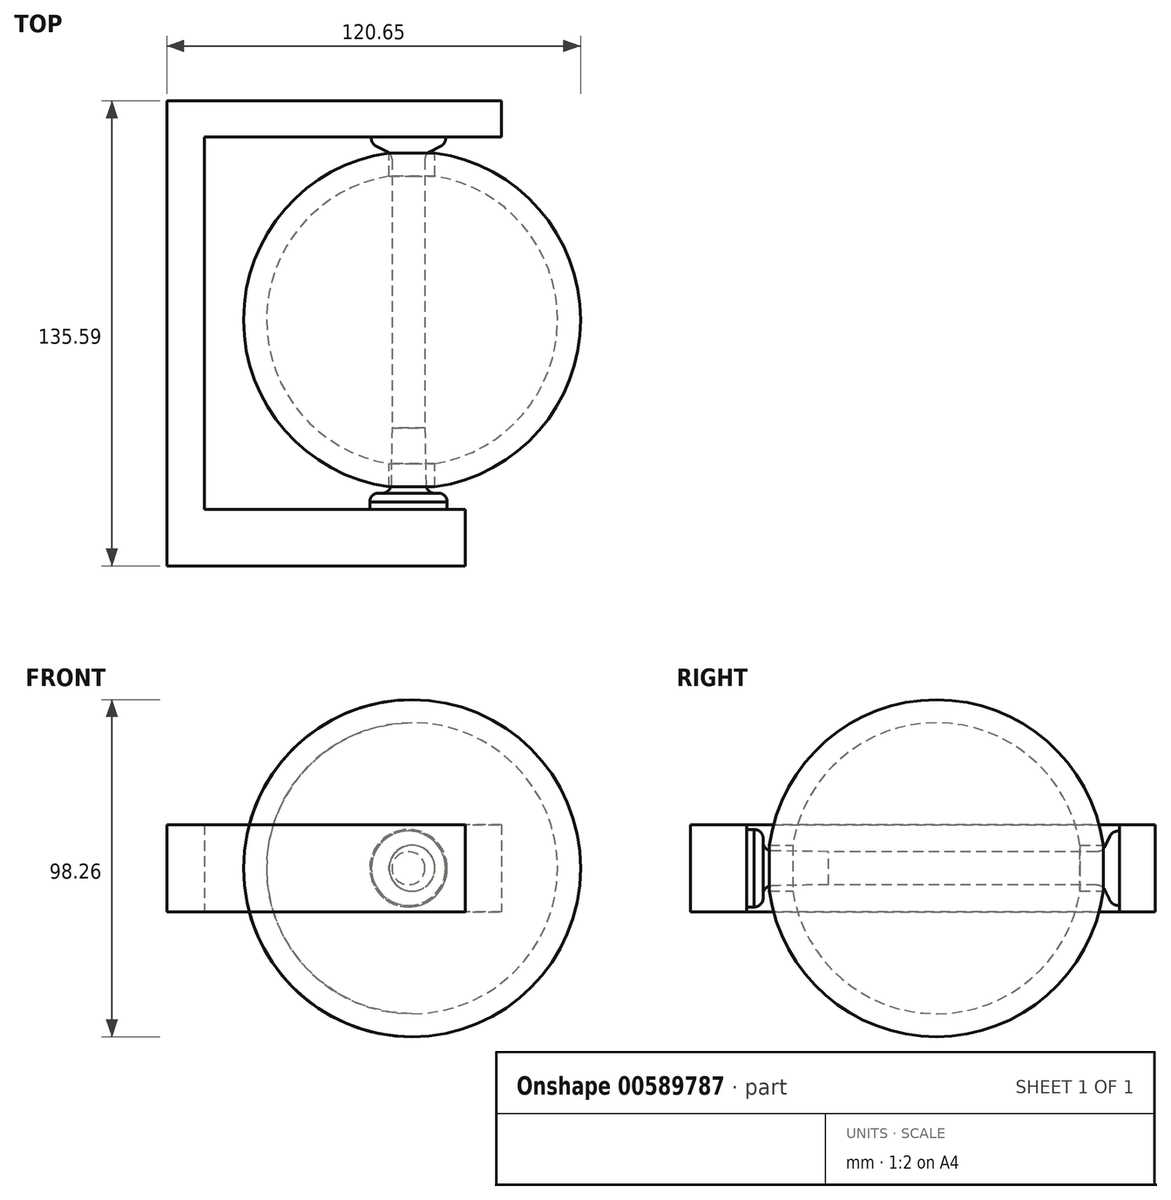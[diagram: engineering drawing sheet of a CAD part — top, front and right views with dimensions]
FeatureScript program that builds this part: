
annotation { "Feature Type Name" : "Feature", "Feature Type Description" : "" }
export const myFeature = defineFeature(function(context is Context, id is Id, definition is map)
    precondition{}
    {
        {
            var Q0;
            Q0=qCreatedBy(makeId("Front.planeOp"),FACE);
            var sketch = newSketch(context, id + "F0", { "sketchPlane" : qUnion([Q0])});
            skArc(sketch, "E0", {"start": v(0, -47.4) * mm, "mid": v(47.4, 0) * mm, "end": v(0, 47.4) * mm});
            skCircle(sketch, "E1", {"center": v(0, 0) * mm, "radius": 42.42 * mm});
            skLineSegment(sketch, "E2.trimOffspring", {"start": v(0, -42.42) * mm, "end": v(0, -47.4) * mm});
            skPoint(sketch, "E3.start.orphan", {"position": v(0, 47.4) * mm});
            skLineSegment(sketch, "E4", {"start": v(0, 47.4) * mm, "end": v(0, 42.42) * mm});
            skCircle(sketch, "E5", {"center": v(0, 0) * mm, "radius": 49.13 * mm});
            skLineSegment(sketch, "E6", {"start": v(0, 47.4) * mm, "end": v(0, 49.13) * mm});
            skLineSegment(sketch, "E7", {"start": v(0, -47.4) * mm, "end": v(0, -49.13) * mm});
            skSolve(sketch);
        }
        {
            var Q0;
            {var subQ4=sQuery(id+"F0.wireOp",EDGE,"E2.trimOffspring");Q0=makeQuery(id+"F0.imprint","IMPRINT",FACE,{"disambiguationData":[TD([[makeQuery(id+"F0.imprint","IMPRINT",EDGE,{"derivedFrom":subQ4}),-1.0]])]});}
            var Q1;
            Q1=sQuery(id+"F0.wireOp",EDGE,"E4");
            revolve(context, id + "F1", {"entities" : qUnion([Q0]), "axis" : qUnion([Q1]), "revolveType" : RevolveType.FULL});
        }
        {
            var Q0;
            Q0=qCreatedBy(makeId("Front.planeOp"),FACE);
            var sketch = newSketch(context, id + "F2", { "sketchPlane" : qUnion([Q0])});
            skCircle(sketch, "E8", {"center": v(0, 0) * mm, "radius": 6.69 * mm});
            skSolve(sketch);
        }
        {
            var Q0;
            Q0 = qSketchRegion(id + "F2", true);
            var Q1;
            Q1=sQuery(id+"F2.wireOp",EDGE,"E8");
            extrude(context, id + "F3", {"entities" : qUnion([Q0]), "operationType" : NewBodyOperationType.REMOVE, "surfaceEntities" : qUnion([Q1]), "endBound" : BoundingType.SYMMETRIC, "depth" : 118.87 * mm, "offsetDistance" : 25.4 * mm});
        }
        {
            var Q0;
            Q0=qCreatedBy(makeId("Top.planeOp"),FACE);
            var sketch = newSketch(context, id + "F4", { "sketchPlane" : qUnion([Q0])});
            skLineSegment(sketch, "E9", {"start": v(15.54, -66.32) * mm, "end": v(15.54, -55.32) * mm});
            skLineSegment(sketch, "E10", {"start": v(15.54, -55.32) * mm, "end": v(-60.54, -55.32) * mm});
            skLineSegment(sketch, "E11", {"start": v(-60.54, -55.32) * mm, "end": v(-60.54, 53.34) * mm});
            skLineSegment(sketch, "E12", {"start": v(-60.54, 53.34) * mm, "end": v(26.1, 53.34) * mm});
            skLineSegment(sketch, "E13", {"start": v(26.1, 53.34) * mm, "end": v(26.1, 63.84) * mm});
            skLineSegment(sketch, "E14", {"start": v(26.1, 63.84) * mm, "end": v(-71.52, 63.84) * mm});
            skLineSegment(sketch, "E15", {"start": v(-71.52, 63.84) * mm, "end": v(-71.52, -71.75) * mm});
            skLineSegment(sketch, "E16", {"start": v(-71.52, -71.75) * mm, "end": v(15.54, -71.75) * mm});
            skLineSegment(sketch, "E17", {"start": v(15.54, -71.75) * mm, "end": v(15.54, -66.32) * mm});
            skSolve(sketch);
        }
        {
            var Q0;
            Q0=qCreatedBy(makeId("Top.planeOp"),FACE);
            var sketch = newSketch(context, id + "F5", { "sketchPlane" : qUnion([Q0])});
            skLineSegment(sketch, "E18", {"start": v(-5.85, 46.79) * mm, "end": v(-5.85, 0) * mm});
            skLineSegment(sketch, "E19", {"start": v(-1.05, 53.56) * mm, "end": v(-11.88, 53.56) * mm});
            skLineSegment(sketch, "E20", {"start": v(-11.88, 53.56) * mm, "end": v(-11.88, 52.93) * mm});
            skLineSegment(sketch, "E21", {"start": v(-10.47, 50.65) * mm, "end": v(-7.26, 49.06) * mm});
            skPoint(sketch, "E22.visualSharp", {"position": v(-5.85, 48.36) * mm});
            skArc(sketch, "E22.filletArc", {"start": v(-5.85, 46.79) * mm, "mid": v(-6.23, 48.13) * mm, "end": v(-7.26, 49.06) * mm});
            skPoint(sketch, "E23.visualSharp", {"position": v(-11.88, 51.35) * mm});
            skArc(sketch, "E23.filletArc", {"start": v(-11.88, 52.93) * mm, "mid": v(-11.5, 51.59) * mm, "end": v(-10.47, 50.65) * mm});
            skLineSegment(sketch, "E24", {"start": v(-5.85, 0) * mm, "end": v(-5.85, -31.5) * mm});
            skLineSegment(sketch, "E25", {"start": v(-1.05, -34.05) * mm, "end": v(-1.05, 53.56) * mm});
            skPoint(sketch, "E26.start.orphan", {"position": v(3.76, -36.6) * mm});
            skLineSegment(sketch, "E27", {"start": v(-5.85, -31.5) * mm, "end": v(-6.13, -48.03) * mm});
            skLineSegment(sketch, "E28", {"start": v(-8.68, -50.53) * mm, "end": v(-9.78, -50.52) * mm});
            skLineSegment(sketch, "E29", {"start": v(-1.05, -56.84) * mm, "end": v(-1.05, -34.05) * mm});
            skPoint(sketch, "E30.visualSharp", {"position": v(-6.17, -50.53) * mm});
            skArc(sketch, "E30.filletArc", {"start": v(-8.68, -50.53) * mm, "mid": v(-6.9, -49.8) * mm, "end": v(-6.13, -48.03) * mm});
            skPoint(sketch, "E31.visualSharp", {"position": v(-13.3, -50.51) * mm});
            skArc(sketch, "E31.filletArc", {"start": v(-9.78, -50.52) * mm, "mid": v(-11.61, -51.3) * mm, "end": v(-12.33, -53.14) * mm});
            skLineSegment(sketch, "E32", {"start": v(-12.33, -53.14) * mm, "end": v(-12.33, -57.67) * mm});
            skLineSegment(sketch, "E33", {"start": v(-12.33, -57.67) * mm, "end": v(-1.05, -56.84) * mm});
            skSolve(sketch);
        }
        {
            var Q0;
            Q0=makeQuery(id+"F5.imprint","IMPRINT",FACE,{"disambiguationData":[TD([[makeQuery(id+"F5.imprint","IMPRINT",EDGE,{"derivedFrom":sQuery(id+"F5.wireOp",EDGE,"E18")}),1.0]])]});
            var Q1;
            Q1=sQuery(id+"F5.wireOp",EDGE,"E25");
            revolve(context, id + "F6", {"operationType" : NewBodyOperationType.ADD, "entities" : qUnion([Q0]), "axis" : qUnion([Q1]), "revolveType" : RevolveType.FULL});
        }
        {
            var Q0;
            Q0=qCreatedBy(makeId("Top.planeOp"),FACE);
            var sketch = newSketch(context, id + "F7", { "sketchPlane" : qUnion([Q0])});
            skLineSegment(sketch, "E34", {"start": v(-10.26, 49.33) * mm, "end": v(-10.26, 43.96) * mm});
            skLineSegment(sketch, "E35", {"start": v(-10.26, 49.33) * mm, "end": v(-10.26, 43.45) * mm});
            skLineSegment(sketch, "E36", {"start": v(-10.26, 43.45) * mm, "end": v(-10.26, 46.64) * mm});
            skLineSegment(sketch, "E37", {"start": v(-9.52, 43.45) * mm, "end": v(-9.52, 49.33) * mm});
            skLineSegment(sketch, "E38", {"start": v(9.3, 48.48) * mm, "end": v(9.3, 42.6) * mm});
            skLineSegment(sketch, "E39", {"start": v(10.05, 42.6) * mm, "end": v(10.05, 48.48) * mm});
            skLineSegment(sketch, "E40", {"start": v(-7.38, 48.48) * mm, "end": v(-7.38, 42.6) * mm});
            skLineSegment(sketch, "E41", {"start": v(-6.63, 42.6) * mm, "end": v(-6.63, 48.48) * mm});
            skLineSegment(sketch, "E42", {"start": v(14.43, 47.63) * mm, "end": v(14.43, 41.75) * mm});
            skLineSegment(sketch, "E43", {"start": v(15.18, 41.75) * mm, "end": v(15.18, 47.63) * mm});
            skSolve(sketch);
        }
        {
            var Q0;
            Q0 = qSketchRegion(id + "F7", true);
            var Q1;
            Q1=makeQuery(id+"F4.imprint","IMPRINT",FACE,{"disambiguationData":[TD([[makeQuery(id+"F4.imprint","IMPRINT",EDGE,{"derivedFrom":sQuery(id+"F4.wireOp",EDGE,"E9")}),1.0]])]});
            extrude(context, id + "F8", {"entities" : qUnion([Q0, Q1]), "operationType" : NewBodyOperationType.ADD, "endBound" : BoundingType.SYMMETRIC, "depth" : 25.4 * mm, "offsetDistance" : 25.4 * mm});
        }
    });
